# Revit family: O5DM-NRG
name_source: partatom
category: Mechanical Equipment
units: mm (PartAtom-declared; Revit-internal decimal feet)

## family parameters
Always vertical = Yes
Cut with Voids When Loaded = No
OmniClass Number = 23.40.40.11.17
OmniClass Title = Refrigerated Cases
Part Type = Normal
Room Calculation Point = No
Round Connector Dimension = Use Radius
Shared = No
Work Plane-Based = Yes

## types (44) — shared parameters
24" Shelf = Yes
BOTTOM ELECTRICAL = Yes
BOTTOM REFRIGERATION PIPING = Yes
Certifications = NSF 7, UL471, CSA
DATE = 05/02/2016
DRAIN PIPING = Yes
Default Elevation = 48"
Defrosts Per Day = 6
Description = Multi-Deck Merchandiser
Discharge Air Velocity (FPM) = 140 FPM
EQUIPMENT DESCRIPTION = Multi-Deck Merchandiser
EQUIPMENT MARK = O5DM-NRG
GLASS = Glass
Height = 81 5/8"
High Power (Cornice) Amps = 0 A
Item Description = Multi-Deck Merchandiser
Legend Number = O5DM-NRG
Manufacturer = HILL PHOENIX
Model = O5DM-NRG
PAINTED METAL UPPER SHELF = PAINTED SHELVES
REAR REFRIGERATION PIPING = Yes
REFRIGERATION PIPING = COPPER PIPE
Refgn = 28 5/8"
Standard Power Amps = 0 A
Superheat Set Point @ Bulb (°F) = 6-8 °F
TOP ELECTRICAL = Yes
Timed-Off Defrost Termination Temp = 42 °F
URL = http://www.hillphoenix.com
Width = 43 1/4"

## per-type parameters (varying)
| type | Application Discipline | BTUH Conventional | BTUH Parallel | CENTER LINE | DRAIN LINE | Discharge Air (°F) | Evaporator (°F) | High Efficiency Amps | High Efficiency Watts | High Power (Cornice) Watts | Length | Length of Cases | Light Length | Lights Per Row | Lights per row | Number of Fans | Standard Power Watts | TOP REFRIGERATION PIPING | Timed-Off Defrost Fail-Safe (Min) |
| 06' Dairy/Deli/Cut Produce with Std. Dairy Sill | Beverage/Bulk Produce with 2.5" Extended Sill | 1023 | 895 | 72" | 192" | 37 °F | 34 °F | 1 A | 53 W | 45 W | 144" | 144" | 4' | 3 |  | 3 | 18 W | Yes | 40 (Min) |
| 08' Dairy/Deli/Cut Produce with Std. Dairy Sill | Dairy/Deli/Cut Produce with Std. Dairy Sill | 1303 | 1140 | 48" | 48" | 31 °F | 28 °F | 0 A | 35 W | 30 W | 96" | 96" | 4' | 2 |  | 2 | 12 W | Yes | 40 (Min) |
| 12' Dairy/Deli/Cut Produce with Std. Dairy Sill | Dairy/Deli/Cut Produce with Std. Dairy Sill | 1303 | 1140 | 72" | 72" | 31 °F | 28 °F | 1 A | 53 W | 45 W | 144" | 144" | 4' | 3 |  | 3 | 18 W | No | 40 (Min) |
| 06' Dairy/Deli/Cut Produce with 2.5" Extended Sill | Dairy/Deli/Cut Produce with 2.5" Extended Sill | 1263 | 1105 | 36" | 36" | 31 °F | 28 °F | 0 A | 35 W | 24 W | 72" | 72" | 3' | 2 |  | 2 | 9 W | Yes | 40 (Min) |
| 08' Dairy/Deli/Cut Produce with 2.5" Extended Sill | Dairy/Deli/Cut Produce with 2.5" Extended Sill | 1263 | 1105 | 48" | 48" | 31 °F | 28 °F | 0 A | 35 W | 30 W | 96" | 96" | 4' | 2 |  | 2 | 12 W | Yes | 40 (Min) |
| 12' Dairy/Deli/Cut Produce with 2.5" Extended Sill | Dairy/Deli/Cut Produce with 2.5" Extended Sill | 1263 | 1105 | 72" | 72" | 31 °F | 28 °F | 1 A | 53 W | 45 W | 144" | 144" | 4' | 3 |  | 3 | 18 W | Yes | 40 (Min) |
| 06' Dairy/Deli/Cut Produce with 5" Extended Sill | Dairy/Deli/Cut Produce with 5" Extended Sill | 1234 | 1080 | 36" | 36" | 31 °F | 28 °F | 0 A | 35 W | 24 W | 72" | 72" | 3' | 2 |  | 2 | 9 W | Yes | 40 (Min) |
| 08' Dairy/Deli/Cut Produce with 5" Extended Sill | Dairy/Deli/Cut Produce with 5" Extended Sill | 1234 | 1080 | 48" | 48" | 31 °F | 28 °F | 0 A | 35 W | 43 W | 96" | 96" | 4' | 2 |  | 2 | 24 W | Yes | 40 (Min) |
| 12' Dairy/Deli/Cut Produce with 5" Extended Sill | Dairy/Deli/Cut Produce with 5" Extended Sill | 1234 | 1080 | 72" | 72" | 31 °F | 28 °F | 1 A | 53 W | 45 W | 144" | 144" | 4' | 3 |  | 3 | 18 W | Yes | 40 (Min) |
| 06' Dairy/Deli/Cut Produce with 7.5" Extended Sill | Dairy/Deli/Cut Produce with 7.5" Extended Sill | 1211 | 1060 | 36" | 36" | 31 °F | 28 °F | 0 A | 35 W | 24 W | 72" | 72" | 3' | 2 |  | 2 | 9 W | Yes | 40 (Min) |
| 08' Dairy/Deli/Cut Produce with 7.5" Extended Sill | Dairy/Deli/Cut Produce with 7.5" Extended Sill | 1211 | 1060 | 48" | 48" | 3100 °F | 28 °F | 0 A | 35 W | 30 W | 96" | 96" | 4' | 2 |  | 2 | 12 W | Yes | 40 (Min) |
| 12' Dairy/Deli/Cut Produce with 7.5" Extended Sill | Dairy/Deli/Cut Produce with 7.5" Extended Sill | 1211 | 1060 | 72" | 72" | 31 °F | 28 °F | 1 A | 53 W | 45 W | 144" | 144" | 4' | 3 |  | 3 | 18 W | Yes | 40 (Min) |
| 06' Beverage/Bulk Produce with Std. Dairy Sill | Beverage/Bulk Produce with Std. Dairy Sill | 1062 | 930 | 36" | 36" | 37 °F | 34 °F | 0 A | 35 W | 24 W | 72" | 72" | 3' | 2 |  | 2 | 9 W | Yes | 40 (Min) |
| 08' Beverage/Bulk Produce with Std. Dairy Sill | Beverage/Bulk Produce with Std. Dairy Sill | 1062 | 930 | 48" | 48" | 37 °F | 34 °F | 0 A | 35 W | 30 W | 96" | 96" | 4' | 2 |  | 2 | 12 W | Yes | 40 (Min) |
| 12' Beverage/Bulk Produce with Std. Dairy Sill | Beverage/Bulk Produce with Std. Dairy Sill | 1062 | 930 | 72" | 48" | 37 °F | 34 °F | 1 A | 53 W | 45 W | 144" | 144" | 4' | 3 |  | 3 | 18 W | Yes | 40 (Min) |
| 06' Beverage/Bulk Produce with 2.5" Extended Sill | Beverage/Bulk Produce with 2.5" Extended Sill | 1023 | 895 | 36" | 36" | 37 °F | 34 °F | 0 A | 35 W | 24 W | 72" | 72" | 3' | 2 |  | 2 | 9 W | Yes | 40 (Min) |
| 08' Beverage/Bulk Produce with 2.5" Extended Sill | Beverage/Bulk Produce with 2.5" Extended Sill | 1023 | 895 | 48" | 48" | 37 °F | 34 °F | 0 A | 35 W | 30 W | 96" | 96" | 4' | 2 |  | 2 | 12 W | Yes | 40 (Min) |
| 12' Beverage/Bulk Produce with 2.5" Extended Sill | Beverage/Bulk Produce with 2.5" Extended Sill | 1023 | 895 | 72" | 192" | 37 °F | 34 °F | 1 A | 53 W | 45 W | 144" | 144" | 4' | 3 |  | 3 | 18 W | Yes | 40 (Min) |
| 06' Beverage/Bulk Produce with 5" Extended Sill | Beverage/Bulk Produce with 5" Extended Sill | 994 | 870 | 36" | 36" | 37 °F | 34 °F | 0 A | 35 W | 24 W | 72" | 72" | 3' | 2 |  | 2 | 9 W | Yes | 40 (Min) |
| 08' Beverage/Bulk Produce with 5" Extended Sill | Beverage/Bulk Produce with 5" Extended Sill | 994 | 870 | 48" | 48" | 37 °F | 34 °F | 0 A | 35 W | 30 W | 96" | 96" | 4' | 2 |  | 2 | 12 W | Yes | 40 (Min) |
| 12' Beverage/Bulk Produce with 5" Extended Sill | Beverage/Bulk Produce with 5" Extended Sill | 994 | 870 | 72" | 48" | 37 °F | 34 °F | 1 A | 53 W | 45 W | 144" | 144" | 4' | 3 |  | 3 | 18 W | Yes | 40 (Min) |
| 06' Beverage/Bulk Produce with 7.5" Extended Sill | Beverage/Bulk Produce with 7.5" Extended Sill | 972 | 850 | 36" | 36" | 37 °F | 34 °F | 0 A | 35 W | 24 W | 72" | 72" | 3' | 2 |  | 2 | 9 W | Yes | 40 (Min) |
| 08' Beverage/Bulk Produce with 7.5" Extended Sill | Beverage/Bulk Produce with 7.5" Extended Sill | 972 | 850 | 48" | 48" | 37 °F | 34 °F | 0 A | 35 W | 30 W | 96" | 96" | 4' | 2 |  | 2 | 12 W | Yes | 40 (Min) |
| 12' Beverage/Bulk Produce with 7.5" Extended Sill | Beverage/Bulk Produce with 7.5" Extended Sill | 972 | 850 | 72" | 48" | 37 °F | 34 °F | 1 A | 53 W | 45 W | 144" | 144" | 4' | 3 |  | 3 | 18 W | Yes | 40 (Min) |
| 12' | Dairy/Deli/Cut Produce | 1211 | 1060 | 72" | 72" | 31 °F | 28 °F | 1 A | 53 W | 45 W | 144" | 48" | 4' | 3 | 3 | 3 | 18 W | Yes | 40 (Min) |
| 8' | Dairy/Deli/Cut Produce | 1234 | 1080 | 48" | 48" | 31 °F | 28 °F | 0 A | 35 W | 30 W | 96" | 48" | 4' | 2 | 2 | 2 | 12 W | Yes | 40 (Min) |
| 6' | Beverage/ Bulk Produce | 1263 | 1105 | 36" | 36" | 31 °F | 28 °F | 0 A | 35 W | 24 W | 72" | 48" | 3' | 2 | 2 | 2 | 9 W | Yes | 40 (Min) |
| 10' | Dairy/Deli/Cut Produce | 1234 | 1080 | 60" | 48" | 31 °F | 28 °F | 1 A | 53 W | 45 W | 120" | 120" | 1'-4' | 2 | 3 | 3 | 18 W | Yes | 40 (Min) |
| 10' BULK EX 2.5 | Dairy/Deli/Cut Produce | 1234 | 1080 | 60" | 48" | 31 °F | 28 °F | 0 A | 35 W | 30 W | 120" | 120" | 4' | 2 |  | 2 | 12 W | Yes | 40 (Min) |
| 10' BULK EX 7.5 | Dairy/Deli/Cut Produce | 1234 | 1080 | 60" | 48" | 31 °F | 28 °F | 0 A | 35 W | 30 W | 120" | 120" | 4' | 2 |  | 2 | 12 W | Yes | 40 (Min) |
| 10' BULK EX 5 | Dairy/Deli/Cut Produce | 1234 | 1080 | 60" | 48" | 31 °F | 28 °F | 0 A | 35 W | 30 W | 120" | 120" | 4' | 2 |  | 2 | 12 W | Yes | 40 (Min) |
| 10' BULK STANDARD | Dairy/Deli/Cut Produce | 1234 | 1080 | 60" | 48" | 31 °F | 28 °F | 0 A | 35 W | 30 W | 120" | 120" | 4' | 2 |  | 2 | 12 W | Yes | 40 (Min) |
| 10' CUT EX 2.5 | Dairy/Deli/Cut Produce | 1234 | 1080 | 60" | 48" | 31 °F | 28 °F | 0 A | 35 W | 30 W | 120" | 120" | 4' | 2 |  | 2 | 12 W | Yes | 40 (Min) |
| 10' CUT EX 7.5 | Dairy/Deli/Cut Produce | 1234 | 1080 | 60" | 48" | 31 °F | 28 °F | 0 A | 35 W | 30 W | 120" | 120" | 4' | 2 |  | 2 | 12 W | Yes | 40 (Min) |
| 10' CUT EX 5 | Dairy/Deli/Cut Produce | 1234 | 1080 | 60" | 48" | 31 °F | 28 °F | 0 A | 35 W | 30 W | 120" | 120" | 4' | 2 |  | 2 | 12 W | Yes | 40 (Min) |
| 10' CUT STANDARD | Dairy/Deli/Cut Produce | 1234 | 1080 | 60" | 48" | 31 °F | 28 °F | 0 A | 35 W | 30 W | 120" | 120" | 4' | 2 | 2-3 | 2 | 12 W | Yes | 40 (Min) |
| 4' | Dairy/Deli/Cut Produce | 1234 | 1080 | 24" | 48" | 31 °F | 28 °F | 0 A | 35 W | 30 W | 48" | 48" | 4' | 2 | 2 | 2 | 12 W | Yes | 40 (Min) |
| 04' Dairy/Deli/Cut Produce with 7.5" Extended Sill | Dairy/Deli/Cut Produce | 1211 | 1060 | 24" | 36" | 31 °F | 28 °F | 0 A | 18 W | 15 W | 48" | 48" | 4' | 1 | 1 | 1 | 6 W | Yes | 40 |
| OS 45 WEDGE LEFT | Dairy/Deli/Cut Produce | 1234 | 1080 | 24" | 48" | 31 °F | 28 °F | 0 A | 35 W | 30 W | 48" | 48" | 4' | 2 | 2 | 2 | 12 W | Yes | 40 (Min) |
| OS 45 WEDGE RIGHT | Dairy/Deli/Cut Produce | 1234 | 1080 | 24" | 48" | 31 °F | 28 °F | 0 A | 35 W | 30 W | 48" | 48" | 4' | 2 | 2 | 2 | 12 W | Yes | 40 (Min) |
| OS 90 WEDGE LEFT | Dairy/Deli/Cut Produce | 1234 | 1080 | 24" | 48" | 31 °F | 28 °F | 0 A | 35 W | 30 W | 48" | 48" | 4' | 2 | 2 | 2 | 12 W | Yes | 40 (Min) |
| OS 90 WEDGE RIGHT | Dairy/Deli/Cut Produce | 1234 | 1080 | 24" | 48" | 31 °F | 28 °F | 0 A | 35 W | 30 W | 48" | 48" | 4' | 2 | 2 | 2 | 12 W | Yes | 40 (Min) |
| IS 45 WEDGE LEFT | Dairy/Deli/Cut Produce | 1234 | 1080 | 24" | 48" | 31 °F | 28 °F | 0 A | 35 W | 30 W | 48" | 48" | 4' | 2 | 2 | 2 | 12 W | Yes | 40 (Min) |
| IS 45 WEDGE RIGHT | Dairy/Deli/Cut Produce | 1234 | 1080 | 24" | 48" | 31 °F | 28 °F | 0 A | 35 W | 30 W | 48" | 48" | 4' | 2 | 2 | 2 | 12 W | Yes | 40 (Min) |

type visibility flags (boolean, named after types; folded from table):
- 06' Dairy/Deli/Cut Produce with Std. Dairy Sill: Yes: (none)
- 08' Dairy/Deli/Cut Produce with Std. Dairy Sill: Yes: (none)
- 12' Dairy/Deli/Cut Produce with Std. Dairy Sill: Yes: (none)
- 06' Dairy/Deli/Cut Produce with 2.5" Extended Sill: Yes: (none)
- 08' Dairy/Deli/Cut Produce with 2.5" Extended Sill: Yes: (none)
- 12' Dairy/Deli/Cut Produce with 2.5" Extended Sill: Yes: (none)
- 06' Dairy/Deli/Cut Produce with 5" Extended Sill: Yes: (none)
- 08' Dairy/Deli/Cut Produce with 5" Extended Sill: Yes: (none)
- 12' Dairy/Deli/Cut Produce with 5" Extended Sill: Yes: (none)
- 06' Dairy/Deli/Cut Produce with 7.5" Extended Sill: Yes: (none)
- 08' Dairy/Deli/Cut Produce with 7.5" Extended Sill: Yes: (none)
- 12' Dairy/Deli/Cut Produce with 7.5" Extended Sill: Yes: (none)
- 06' Beverage/Bulk Produce with Std. Dairy Sill: Yes: (none)
- 08' Beverage/Bulk Produce with Std. Dairy Sill: Yes: (none)
- 12' Beverage/Bulk Produce with Std. Dairy Sill: Yes: (none)
- 06' Beverage/Bulk Produce with 2.5" Extended Sill: Yes: (none)
- 08' Beverage/Bulk Produce with 2.5" Extended Sill: Yes: (none)
- 12' Beverage/Bulk Produce with 2.5" Extended Sill: Yes: (none)
- 06' Beverage/Bulk Produce with 5" Extended Sill: Yes: (none)
- 08' Beverage/Bulk Produce with 5" Extended Sill: Yes: (none)
- 12' Beverage/Bulk Produce with 5" Extended Sill: Yes: (none)
- 06' Beverage/Bulk Produce with 7.5" Extended Sill: Yes: (none)
- 08' Beverage/Bulk Produce with 7.5" Extended Sill: Yes: (none)
- 12' Beverage/Bulk Produce with 7.5" Extended Sill: Yes: (none)
- 12': Yes: (none)
- 8': Yes: (none)
- 6': Yes: (none)
- 10': Yes: (none)
- 10' BULK EX 2.5: Yes: (none)
- 10' BULK EX 7.5: Yes: (none)
- 10' BULK EX 5: Yes: (none)
- 10' BULK STANDARD: Yes: (none)
- 10' CUT EX 2.5: Yes: (none)
- 10' CUT EX 7.5: Yes: (none)
- 10' CUT EX 5: Yes: (none)
- 10' CUT STANDARD: Yes: (none)
- 4': Yes: (none)
- 04' Dairy/Deli/Cut Produce with 7.5" Extended Sill: Yes: (none)
- OS 45 WEDGE LEFT: Yes: OS 45 WEDGE LEFT
- OS 45 WEDGE RIGHT: Yes: (none)
- OS 90 WEDGE LEFT: Yes: (none)
- OS 90 WEDGE RIGHT: Yes: (none)
- IS 45 WEDGE LEFT: Yes: (none)
- IS 45 WEDGE RIGHT: Yes: (none)

## geometry (parser evidence)
native form markers: Blend x17, Sweep x14
no freeform markers — native parametric forms only
